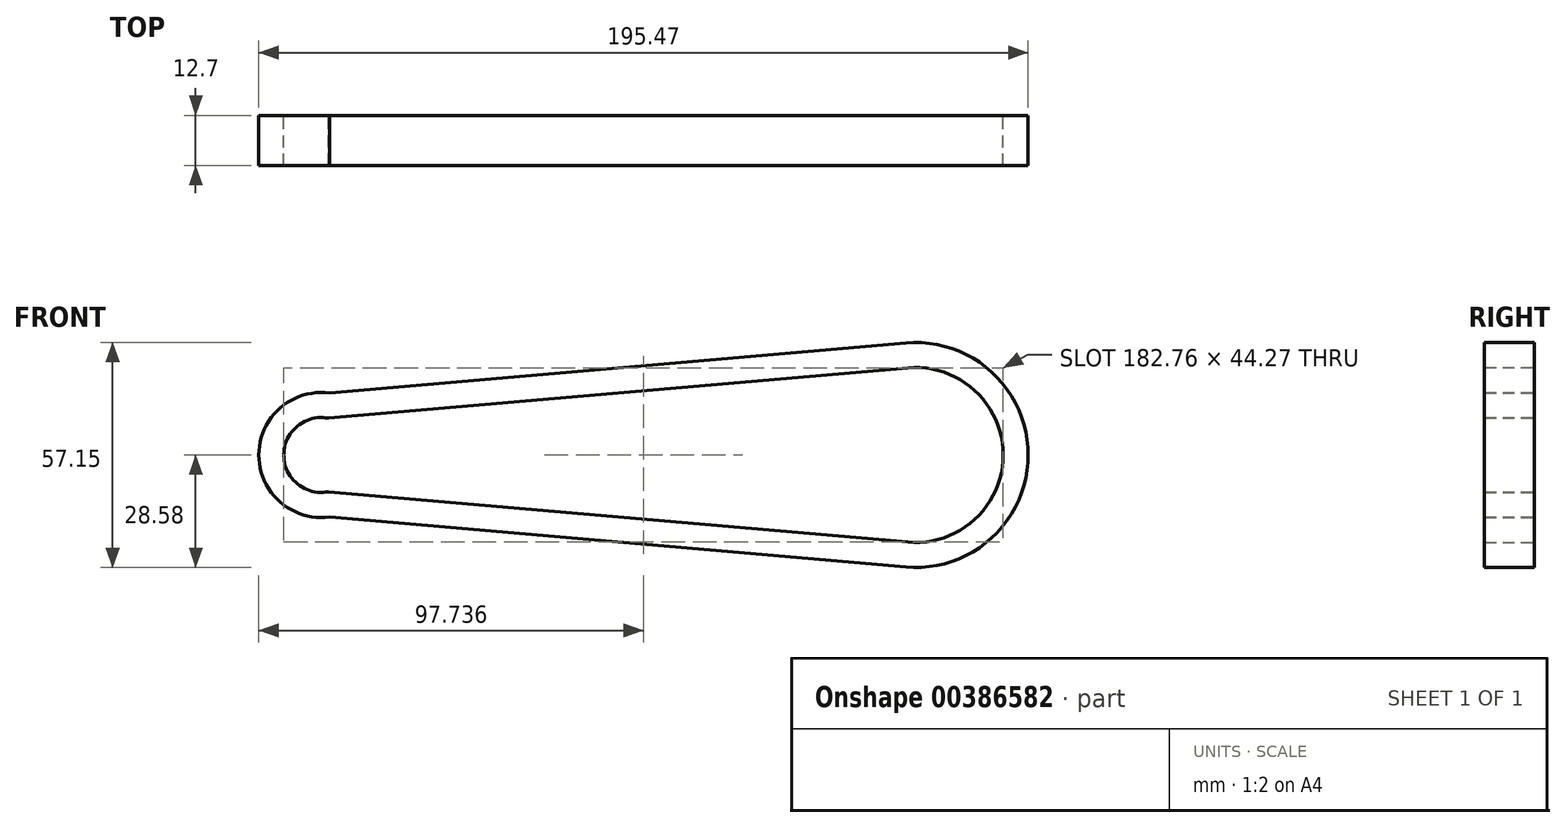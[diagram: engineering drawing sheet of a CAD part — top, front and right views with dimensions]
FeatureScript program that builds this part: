
annotation { "Feature Type Name" : "Feature", "Feature Type Description" : "" }
export const myFeature = defineFeature(function(context is Context, id is Id, definition is map)
    precondition{}
    {
        {
            var Q0;
            Q0=qCreatedBy(makeId("Front.planeOp"),FACE);
            var sketch = newSketch(context, id + "F0", { "sketchPlane" : qUnion([Q0])});
            skArc(sketch, "E0", {"start": v(-3.36, -22.14) * mm, "mid": v(20.84, 0) * mm, "end": v(-3.36, 22.14) * mm});
            skArc(sketch, "E1", {"start": v(-150.55, 9.34) * mm, "mid": v(-161.93, 0) * mm, "end": v(-150.55, -9.34) * mm});
            skLineSegment(sketch, "E2", {"start": v(-152.4, 0) * mm, "end": v(0, 0) * mm});
            skLineSegment(sketch, "E3", {"start": v(-3.36, 22.14) * mm, "end": v(-150.55, 9.34) * mm});
            skLineSegment(sketch, "E4.MirrorCS", {"start": v(-3.36, -22.14) * mm, "end": v(-150.55, -9.34) * mm});
            skLineSegment(sketch, "E5.0", {"start": v(-3.91, 28.46) * mm, "end": v(-150.32, 15.74) * mm});
            skArc(sketch, "E5.1", {"start": v(-3.91, -28.46) * mm, "mid": v(27.19, 0) * mm, "end": v(-3.91, 28.46) * mm});
            skLineSegment(sketch, "E5.2", {"start": v(-3.91, -28.46) * mm, "end": v(-150.32, -15.74) * mm});
            skArc(sketch, "E5.3", {"start": v(-150.32, 15.74) * mm, "mid": v(-168.28, 0) * mm, "end": v(-150.32, -15.74) * mm});
            skSolve(sketch);
        }
        {
            var Q0;
            Q0 = qSketchRegion(id + "F0", true);
            extrude(context, id + "F1", {"entities" : qUnion([Q0]), "depth" : 12.7 * mm});
        }
    });
